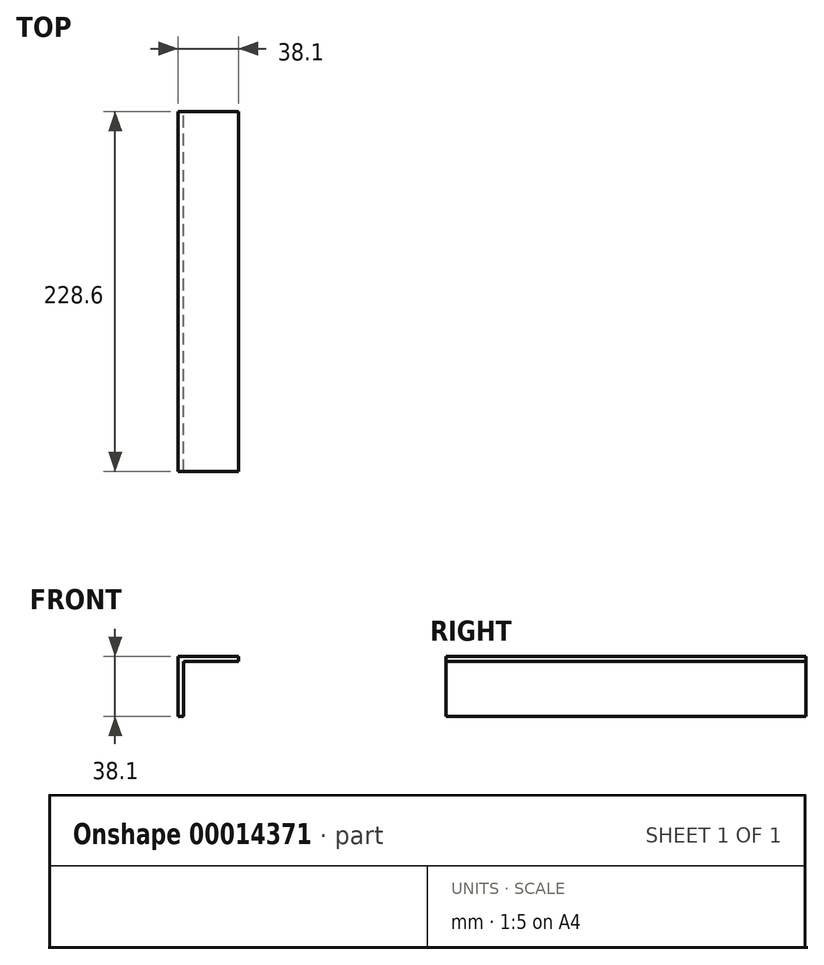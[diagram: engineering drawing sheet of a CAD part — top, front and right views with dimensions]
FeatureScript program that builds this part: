
annotation { "Feature Type Name" : "Feature", "Feature Type Description" : "" }
export const myFeature = defineFeature(function(context is Context, id is Id, definition is map)
    precondition{}
    {
        {
            var Q0;
            Q0=qCreatedBy(makeId("Front.planeOp"),FACE);
            var sketch = newSketch(context, id + "F0", { "sketchPlane" : qUnion([Q0])});
            skLineSegment(sketch, "E0", {"start": v(0, 0) * mm, "end": v(0, -34.93) * mm});
            skLineSegment(sketch, "E1", {"start": v(0, 0) * mm, "end": v(34.92, 0) * mm});
            skLineSegment(sketch, "E2.0", {"start": v(-3.18, 3.17) * mm, "end": v(-3.17, -34.93) * mm});
            skLineSegment(sketch, "E2.1", {"start": v(-3.18, 3.18) * mm, "end": v(34.92, 3.18) * mm});
            skLineSegment(sketch, "E3", {"start": v(-3.17, -34.93) * mm, "end": v(0, -34.93) * mm});
            skLineSegment(sketch, "E4", {"start": v(34.92, 0) * mm, "end": v(34.92, 3.18) * mm});
            skSolve(sketch);
        }
        {
            var Q0;
            Q0=qSketchRegion(id+"F0",true);
            extrude(context, id + "F1", {"entities" : qUnion([Q0]), "depth" : 228.6 * mm});
        }
    });
